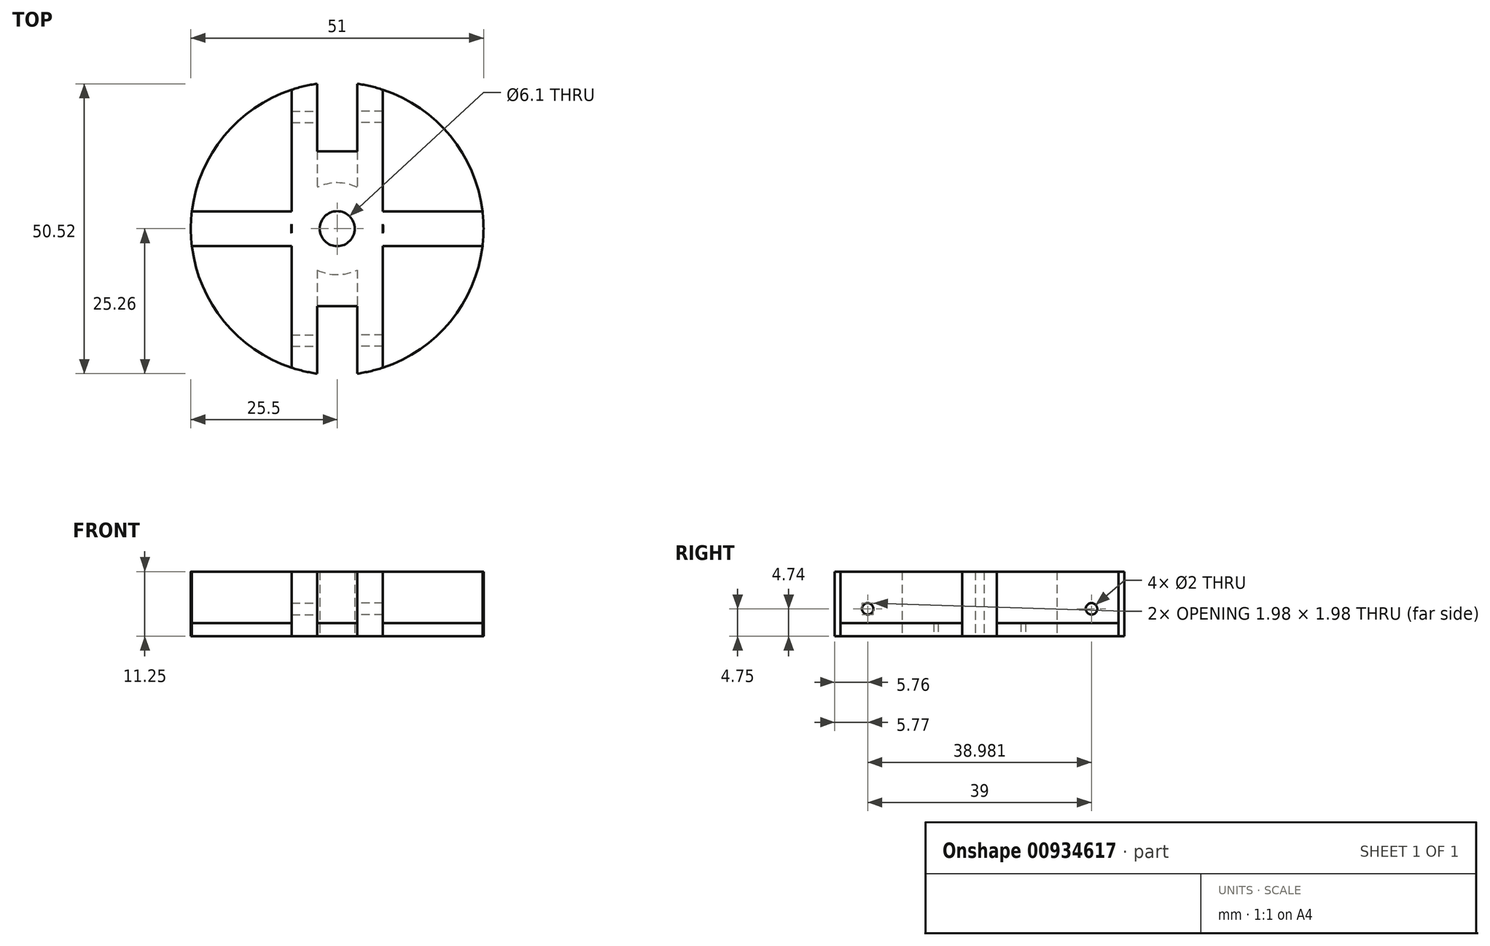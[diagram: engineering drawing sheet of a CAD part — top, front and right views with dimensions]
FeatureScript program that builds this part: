
annotation { "Feature Type Name" : "Feature", "Feature Type Description" : "" }
export const myFeature = defineFeature(function(context is Context, id is Id, definition is map)
    precondition{}
    {
        {
            var Q0;
            Q0=qCreatedBy(makeId("Top.planeOp"),FACE);
            var sketch = newSketch(context, id + "F0", { "sketchPlane" : qUnion([Q0])});
            skCircle(sketch, "E0", {"center": v(0, 0) * mm, "radius": 25.5 * mm});
            skCircle(sketch, "E1", {"center": v(0, 0) * mm, "radius": 3.05 * mm});
            skLineSegment(sketch, "E2", {"start": v(-3.5, 30.59) * mm, "end": v(-3.5, -31.35) * mm});
            skLineSegment(sketch, "E3.MirrorCS", {"start": v(3.5, 30.59) * mm, "end": v(3.5, -31.35) * mm});
            skLineSegment(sketch, "E4", {"start": v(-7.96, 13.5) * mm, "end": v(8.22, 13.5) * mm});
            skLineSegment(sketch, "E5.MirrorCS", {"start": v(-7.96, -13.5) * mm, "end": v(8.22, -13.5) * mm});
            skLineSegment(sketch, "E6", {"start": v(-7.96, -13.5) * mm, "end": v(-7.96, -24.22) * mm});
            skLineSegment(sketch, "E7.MirrorCS", {"start": v(7.96, -13.5) * mm, "end": v(7.96, -24.22) * mm});
            skLineSegment(sketch, "E8.MirrorCS", {"start": v(-7.96, 13.5) * mm, "end": v(-7.96, 24.22) * mm});
            skLineSegment(sketch, "E9.MirrorCS", {"start": v(7.96, 13.5) * mm, "end": v(7.96, 24.22) * mm});
            skCircle(sketch, "E10", {"center": v(0, 0) * mm, "radius": 8 * mm});
            skLineSegment(sketch, "E11", {"start": v(-7.96, 13.5) * mm, "end": v(-7.96, -13.5) * mm});
            skLineSegment(sketch, "E12.MirrorCS", {"start": v(7.96, 13.5) * mm, "end": v(7.96, -13.5) * mm});
            skLineSegment(sketch, "E13", {"start": v(-7.96, 3) * mm, "end": v(-34.21, 3) * mm});
            skLineSegment(sketch, "E14.MirrorCS", {"start": v(-7.96, -3) * mm, "end": v(-34.21, -3) * mm});
            skLineSegment(sketch, "E15.MirrorCS", {"start": v(7.96, 3) * mm, "end": v(34.21, 3) * mm});
            skLineSegment(sketch, "E16.MirrorCS", {"start": v(7.96, -3) * mm, "end": v(34.21, -3) * mm});
            skLineSegment(sketch, "E17", {"start": v(-12, 13.68) * mm, "end": v(13.18, 13.68) * mm, "construction": true});
            skSolve(sketch);
        }
        {
            var Q0;
            {var subQ0=sQuery(id+"F0.wireOp",EDGE,"E10");var subQ1=sQuery(id+"F0.wireOp",EDGE,"E3.MirrorCS");var subQ2=makeQuery(id+"F0.imprint","INTERSECT",VERTEX,{"disambiguationData":[OD(0.0)],"derivedFrom":[subQ1,subQ0]});Q0=makeQuery(id+"F0.imprint","IMPRINT",FACE,{"disambiguationData":[TD([[makeQuery(id+"F0.imprint","IMPRINT",EDGE,{"disambiguationData":[TD([[subQ2,-1.0]])],"derivedFrom":subQ1}),1.0]])]});}
            var Q1;
            Q1=makeQuery(id+"F0.imprint","IMPRINT",FACE,{"disambiguationData":[TD([[makeQuery(id+"F0.imprint","IMPRINT",EDGE,{"derivedFrom":sQuery(id+"F0.wireOp",EDGE,"E1")}),-1.0]])]});
            var Q2;
            {var subQ0=sQuery(id+"F0.wireOp",EDGE,"E10");var subQ1=sQuery(id+"F0.wireOp",EDGE,"E2");var subQ2=makeQuery(id+"F0.imprint","INTERSECT",VERTEX,{"disambiguationData":[OD(0.0)],"derivedFrom":[subQ1,subQ0]});Q2=makeQuery(id+"F0.imprint","IMPRINT",FACE,{"disambiguationData":[TD([[makeQuery(id+"F0.imprint","IMPRINT",EDGE,{"disambiguationData":[TD([[subQ2,-1.0]])],"derivedFrom":subQ1}),-1.0]])]});}
            var Q3;
            {var subQ0=sQuery(id+"F0.wireOp",EDGE,"E8.MirrorCS");Q3=makeQuery(id+"F0.imprint","IMPRINT",FACE,{"disambiguationData":[TD([[makeQuery(id+"F0.imprint","IMPRINT",EDGE,{"derivedFrom":subQ0}),-1.0]])]});}
            var Q4;
            {var subQ0=sQuery(id+"F0.wireOp",EDGE,"E9.MirrorCS");Q4=makeQuery(id+"F0.imprint","IMPRINT",FACE,{"disambiguationData":[TD([[makeQuery(id+"F0.imprint","IMPRINT",EDGE,{"derivedFrom":subQ0}),1.0]])]});}
            var Q5;
            {var subQ0=sQuery(id+"F0.wireOp",EDGE,"E7.MirrorCS");Q5=makeQuery(id+"F0.imprint","IMPRINT",FACE,{"disambiguationData":[TD([[makeQuery(id+"F0.imprint","IMPRINT",EDGE,{"derivedFrom":subQ0}),-1.0]])]});}
            var Q6;
            {var subQ0=sQuery(id+"F0.wireOp",EDGE,"E6");Q6=makeQuery(id+"F0.imprint","IMPRINT",FACE,{"disambiguationData":[TD([[makeQuery(id+"F0.imprint","IMPRINT",EDGE,{"derivedFrom":subQ0}),1.0]])]});}
            var Q7;
            {var subQ0=sQuery(id+"F0.wireOp",EDGE,"E4");var subQ1=sQuery(id+"F0.wireOp",EDGE,"E2");var subQ2=makeQuery(id+"F0.imprint","INTERSECT",VERTEX,{"derivedFrom":[subQ1,subQ0]});Q7=makeQuery(id+"F0.imprint","IMPRINT",FACE,{"disambiguationData":[TD([[makeQuery(id+"F0.imprint","IMPRINT",EDGE,{"disambiguationData":[TD([[subQ2,-1.0]])],"derivedFrom":subQ1}),-1.0]])]});}
            var Q8;
            {var subQ0=sQuery(id+"F0.wireOp",EDGE,"E4");var subQ1=sQuery(id+"F0.wireOp",EDGE,"E3.MirrorCS");var subQ2=makeQuery(id+"F0.imprint","INTERSECT",VERTEX,{"derivedFrom":[subQ1,subQ0]});Q8=makeQuery(id+"F0.imprint","IMPRINT",FACE,{"disambiguationData":[TD([[makeQuery(id+"F0.imprint","IMPRINT",EDGE,{"disambiguationData":[TD([[subQ2,-1.0]])],"derivedFrom":subQ1}),1.0]])]});}
            var Q9;
            {var subQ0=sQuery(id+"F0.wireOp",EDGE,"E10");var subQ1=sQuery(id+"F0.wireOp",EDGE,"E3.MirrorCS");var subQ2=makeQuery(id+"F0.imprint","INTERSECT",VERTEX,{"disambiguationData":[OD(1.0)],"derivedFrom":[subQ1,subQ0]});Q9=makeQuery(id+"F0.imprint","IMPRINT",FACE,{"disambiguationData":[TD([[makeQuery(id+"F0.imprint","IMPRINT",EDGE,{"disambiguationData":[TD([[subQ2,-1.0]])],"derivedFrom":subQ1}),1.0]])]});}
            var Q10;
            {var subQ0=sQuery(id+"F0.wireOp",EDGE,"E10");var subQ1=sQuery(id+"F0.wireOp",EDGE,"E2");var subQ2=makeQuery(id+"F0.imprint","INTERSECT",VERTEX,{"disambiguationData":[OD(1.0)],"derivedFrom":[subQ1,subQ0]});Q10=makeQuery(id+"F0.imprint","IMPRINT",FACE,{"disambiguationData":[TD([[makeQuery(id+"F0.imprint","IMPRINT",EDGE,{"disambiguationData":[TD([[subQ2,-1.0]])],"derivedFrom":subQ1}),-1.0]])]});}
            var Q11;
            {var subQ5=sQuery(id+"F0.wireOp",EDGE,"E13");var subQ8=sQuery(id+"F0.wireOp",EDGE,"E0");var subQ9=makeQuery(id+"F0.imprint","INTERSECT",VERTEX,{"derivedFrom":[subQ8,subQ5]});Q11=makeQuery(id+"F0.imprint","IMPRINT",FACE,{"disambiguationData":[TD([[makeQuery(id+"F0.imprint","IMPRINT",EDGE,{"disambiguationData":[TD([[subQ9,-1.0]])],"derivedFrom":subQ8}),1.0]])]});}
            var Q12;
            {var subQ5=sQuery(id+"F0.wireOp",EDGE,"E15.MirrorCS");var subQ8=sQuery(id+"F0.wireOp",EDGE,"E0");var subQ9=makeQuery(id+"F0.imprint","INTERSECT",VERTEX,{"derivedFrom":[subQ8,subQ5]});Q12=makeQuery(id+"F0.imprint","IMPRINT",FACE,{"disambiguationData":[TD([[makeQuery(id+"F0.imprint","IMPRINT",EDGE,{"disambiguationData":[TD([[subQ9,1.0]])],"derivedFrom":subQ8}),1.0]])]});}
            var Q13;
            {var subQ0=sQuery(id+"F0.wireOp",EDGE,"E10");var subQ1=sQuery(id+"F0.wireOp",EDGE,"E2");var subQ2=makeQuery(id+"F0.imprint","INTERSECT",VERTEX,{"disambiguationData":[OD(1.0)],"derivedFrom":[subQ1,subQ0]});Q13=makeQuery(id+"F0.imprint","IMPRINT",FACE,{"disambiguationData":[TD([[makeQuery(id+"F0.imprint","IMPRINT",EDGE,{"disambiguationData":[TD([[subQ2,-1.0]])],"derivedFrom":subQ1}),1.0]])]});}
            var Q14;
            {var subQ0=sQuery(id+"F0.wireOp",EDGE,"E4");var subQ1=sQuery(id+"F0.wireOp",EDGE,"E2");var subQ2=makeQuery(id+"F0.imprint","INTERSECT",VERTEX,{"derivedFrom":[subQ1,subQ0]});Q14=makeQuery(id+"F0.imprint","IMPRINT",FACE,{"disambiguationData":[TD([[makeQuery(id+"F0.imprint","IMPRINT",EDGE,{"disambiguationData":[TD([[subQ2,-1.0]])],"derivedFrom":subQ1}),1.0]])]});}
            extrude(context, id + "F1", {"entities" : qUnion([Q0, Q1, Q2, Q3, Q4, Q5, Q6, Q7, Q8, Q9, Q10, Q11, Q12, Q13, Q14]), "depth" : 11.25 * mm, "offsetDistance" : 25 * mm});
        }
        {
            var Q0;
            {var subQ9=sQuery(id+"F0.wireOp",EDGE,"E6");Q0=makeQuery(id+"F0.imprint","IMPRINT",FACE,{"disambiguationData":[TD([[makeQuery(id+"F0.imprint","IMPRINT",EDGE,{"derivedFrom":subQ9}),-1.0]])]});}
            var Q1;
            {var subQ0=sQuery(id+"F0.wireOp",EDGE,"E10");var subQ1=sQuery(id+"F0.wireOp",EDGE,"E2");var subQ2=makeQuery(id+"F0.imprint","INTERSECT",VERTEX,{"disambiguationData":[OD(1.0)],"derivedFrom":[subQ1,subQ0]});Q1=makeQuery(id+"F0.imprint","IMPRINT",FACE,{"disambiguationData":[TD([[makeQuery(id+"F0.imprint","IMPRINT",EDGE,{"disambiguationData":[TD([[subQ2,-1.0]])],"derivedFrom":subQ1}),1.0]])]});}
            var Q2;
            {var subQ0=sQuery(id+"F0.wireOp",EDGE,"E4");var subQ1=sQuery(id+"F0.wireOp",EDGE,"E2");var subQ2=makeQuery(id+"F0.imprint","INTERSECT",VERTEX,{"derivedFrom":[subQ1,subQ0]});Q2=makeQuery(id+"F0.imprint","IMPRINT",FACE,{"disambiguationData":[TD([[makeQuery(id+"F0.imprint","IMPRINT",EDGE,{"disambiguationData":[TD([[subQ2,-1.0]])],"derivedFrom":subQ1}),1.0]])]});}
            var Q3;
            {var subQ7=sQuery(id+"F0.wireOp",EDGE,"E7.MirrorCS");Q3=makeQuery(id+"F0.imprint","IMPRINT",FACE,{"disambiguationData":[TD([[makeQuery(id+"F0.imprint","IMPRINT",EDGE,{"derivedFrom":subQ7}),1.0]])]});}
            var Q4;
            {var subQ0=sQuery(id+"F0.wireOp",EDGE,"E9.MirrorCS");Q4=makeQuery(id+"F0.imprint","IMPRINT",FACE,{"disambiguationData":[TD([[makeQuery(id+"F0.imprint","IMPRINT",EDGE,{"derivedFrom":subQ0}),-1.0]])]});}
            var Q5;
            {var subQ0=sQuery(id+"F0.wireOp",EDGE,"E8.MirrorCS");Q5=makeQuery(id+"F0.imprint","IMPRINT",FACE,{"disambiguationData":[TD([[makeQuery(id+"F0.imprint","IMPRINT",EDGE,{"derivedFrom":subQ0}),1.0]])]});}
            extrude(context, id + "F2", {"entities" : qUnion([Q0, Q1, Q2, Q3, Q4, Q5]), "depth" : 2.25 * mm, "offsetDistance" : 25 * mm});
        }
        {
            var Q0;
            Q0=qCreatedBy(makeId("Right.planeOp"),FACE);
            var sketch = newSketch(context, id + "F3", { "sketchPlane" : qUnion([Q0])});
            skLineSegment(sketch, "E18", {"start": v(-32.47, 4.75) * mm, "end": v(32.72, 4.75) * mm, "construction": true});
            skLineSegment(sketch, "E19", {"start": v(-19.5, 20.77) * mm, "end": v(-19.5, -6.96) * mm, "construction": true});
            skPoint(sketch, "E20", {"position": v(-19.5, 4.75) * mm});
            skLineSegment(sketch, "E21.MirrorCS", {"start": v(19.5, 20.77) * mm, "end": v(19.5, -6.96) * mm, "construction": true});
            skPoint(sketch, "E22", {"position": v(19.5, 4.75) * mm});
            skSolve(sketch);
        }
        {
            var Q0;
            Q0=sQuery(id+"F3.wireOp",VERTEX,"E20");
            var Q1;
            Q1=sQuery(id+"F3.wireOp",VERTEX,"E22");
            var Q2;
            Q2=makeQuery(id+"F1.opExtrude","SWEPT_BODY",BODY,{"disambiguationData":[OSD([sQuery(id+"F0.wireOp",EDGE,"E0"),sQuery(id+"F0.wireOp",EDGE,"E1"),sQuery(id+"F0.wireOp",EDGE,"E2"),sQuery(id+"F0.wireOp",EDGE,"E3.MirrorCS"),sQuery(id+"F0.wireOp",EDGE,"E6"),sQuery(id+"F0.wireOp",EDGE,"E7.MirrorCS"),sQuery(id+"F0.wireOp",EDGE,"E8.MirrorCS"),sQuery(id+"F0.wireOp",EDGE,"E9.MirrorCS"),sQuery(id+"F0.wireOp",EDGE,"E10"),sQuery(id+"F0.wireOp",EDGE,"E11"),sQuery(id+"F0.wireOp",EDGE,"E12.MirrorCS"),sQuery(id+"F0.wireOp",EDGE,"E13"),sQuery(id+"F0.wireOp",EDGE,"E14.MirrorCS"),sQuery(id+"F0.wireOp",EDGE,"E15.MirrorCS"),sQuery(id+"F0.wireOp",EDGE,"E16.MirrorCS")])]});
            hole(context, id + "F4", {"style" : HoleStyle.SIMPLE, "endStyle" : HoleEndStyle.THROUGH, "holeDiameter" : 2 * mm, "majorDiameter" : 5 * mm, "isTappedThrough" : true, "tappedDepth" : 12.7 * mm, "tapClearance" : 3, "startFromSketch" : true, "locations" : qUnion([Q0, Q1]), "scope" : qUnion([Q2])});
        }
        {
            var Q0;
            Q0=sQuery(id+"F3.wireOp",VERTEX,"E20");
            var Q1;
            Q1=sQuery(id+"F3.wireOp",VERTEX,"E22");
            var Q2;
            Q2=makeQuery(id+"F1.opExtrude","SWEPT_BODY",BODY,{"disambiguationData":[OSD([sQuery(id+"F0.wireOp",EDGE,"E0"),sQuery(id+"F0.wireOp",EDGE,"E1"),sQuery(id+"F0.wireOp",EDGE,"E2"),sQuery(id+"F0.wireOp",EDGE,"E3.MirrorCS"),sQuery(id+"F0.wireOp",EDGE,"E6"),sQuery(id+"F0.wireOp",EDGE,"E7.MirrorCS"),sQuery(id+"F0.wireOp",EDGE,"E8.MirrorCS"),sQuery(id+"F0.wireOp",EDGE,"E9.MirrorCS"),sQuery(id+"F0.wireOp",EDGE,"E10"),sQuery(id+"F0.wireOp",EDGE,"E11"),sQuery(id+"F0.wireOp",EDGE,"E12.MirrorCS"),sQuery(id+"F0.wireOp",EDGE,"E13"),sQuery(id+"F0.wireOp",EDGE,"E14.MirrorCS"),sQuery(id+"F0.wireOp",EDGE,"E15.MirrorCS"),sQuery(id+"F0.wireOp",EDGE,"E16.MirrorCS")])]});
            hole(context, id + "F5", {"style" : HoleStyle.SIMPLE, "endStyle" : HoleEndStyle.THROUGH, "oppositeDirection" : true, "holeDiameter" : 2 * mm, "majorDiameter" : 5 * mm, "isTappedThrough" : true, "tappedDepth" : 12.7 * mm, "tapClearance" : 3, "startFromSketch" : true, "locations" : qUnion([Q0, Q1]), "scope" : qUnion([Q2])});
        }
    });
